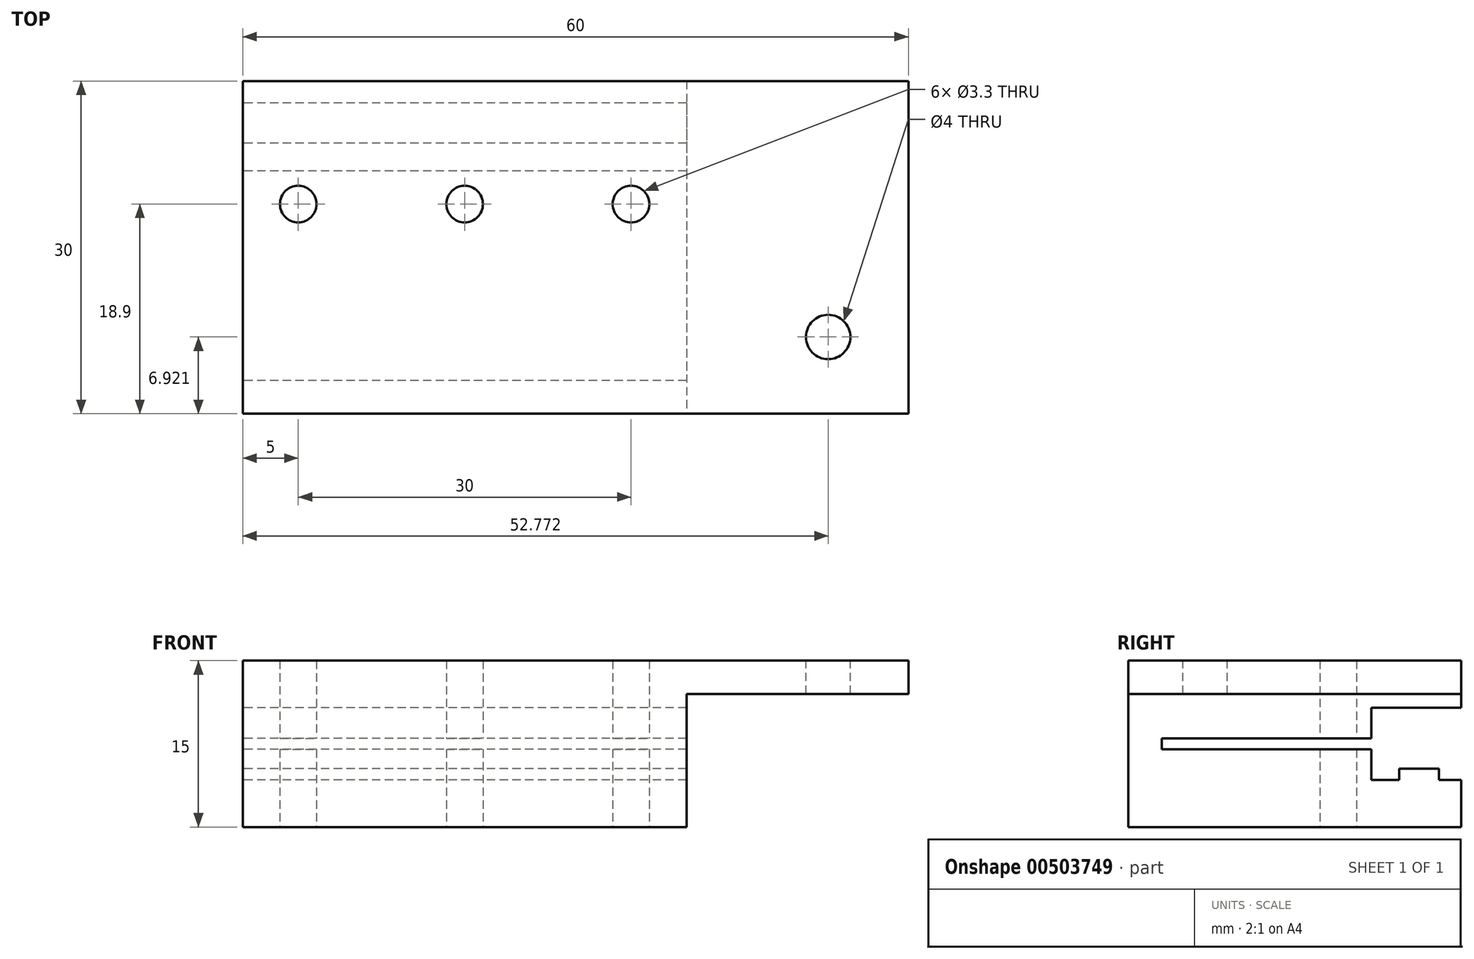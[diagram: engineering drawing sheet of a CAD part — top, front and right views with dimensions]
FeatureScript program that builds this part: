
annotation { "Feature Type Name" : "Feature", "Feature Type Description" : "" }
export const myFeature = defineFeature(function(context is Context, id is Id, definition is map)
    precondition{}
    {
        {
            var Q0;
            Q0=qCreatedBy(makeId("Front.planeOp"),FACE);
            var sketch = newSketch(context, id + "F0", { "sketchPlane" : qUnion([Q0])});
            skLineSegment(sketch, "E0.bottom", {"start": v(30, 7.5) * mm, "end": v(-30, 7.5) * mm});
            skLineSegment(sketch, "E0.top", {"start": v(30, -7.5) * mm, "end": v(-30, -7.5) * mm});
            skLineSegment(sketch, "E0.left", {"start": v(30, 7.5) * mm, "end": v(30, -7.5) * mm});
            skLineSegment(sketch, "E0.right", {"start": v(-30, 7.5) * mm, "end": v(-30, -7.5) * mm});
            skPoint(sketch, "E0.middle", {"position": v(0, 0) * mm});
            skSolve(sketch);
        }
        {
            var Q0;
            Q0 = qSketchRegion(id + "F0", true);
            extrude(context, id + "F1", {"entities" : qUnion([Q0]), "depth" : 30 * mm});
        }
        {
            var Q0;
            Q0=makeQuery(id+"F1.opExtrude","SWEPT_FACE",FACE,{"disambiguationData":[OSD([sQuery(id+"F0.wireOp",EDGE,"E0.right")])]});
            var sketch = newSketch(context, id + "F2", { "sketchPlane" : qUnion([Q0])});
            skLineSegment(sketch, "E1.bottom", {"start": v(0, 3.25) * mm, "end": v(8.1, 3.25) * mm});
            skLineSegment(sketch, "E1.top", {"start": v(0, -3.25) * mm, "end": v(2, -3.25) * mm});
            skLineSegment(sketch, "E1.left", {"start": v(0, 3.25) * mm, "end": v(0, -3.25) * mm});
            skLineSegment(sketch, "E1.right", {"start": v(8.1, 3.25) * mm, "end": v(8.1, 0.5) * mm});
            skLineSegment(sketch, "E2.bottom", {"start": v(8.1, 0.5) * mm, "end": v(27, 0.5) * mm});
            skLineSegment(sketch, "E2.top", {"start": v(8.1, -0.5) * mm, "end": v(27, -0.5) * mm});
            skLineSegment(sketch, "E2.right", {"start": v(27, 0.5) * mm, "end": v(27, -0.5) * mm});
            skLineSegment(sketch, "E3.trimOffspring", {"start": v(8.1, -0.5) * mm, "end": v(8.1, -3.25) * mm});
            skLineSegment(sketch, "E4.top", {"start": v(2, -2.25) * mm, "end": v(5.6, -2.25) * mm});
            skLineSegment(sketch, "E4.left", {"start": v(2, -3.25) * mm, "end": v(2, -2.25) * mm});
            skLineSegment(sketch, "E4.right", {"start": v(5.6, -3.25) * mm, "end": v(5.6, -2.25) * mm});
            skLineSegment(sketch, "E5.trimOffspring", {"start": v(5.6, -3.25) * mm, "end": v(8.1, -3.25) * mm});
            skSolve(sketch);
        }
        {
            var Q0;
            Q0 = qSketchRegion(id + "F2", true);
            extrude(context, id + "F3", {"entities" : qUnion([Q0]), "operationType" : NewBodyOperationType.REMOVE, "endBound" : BoundingType.THROUGH_ALL, "oppositeDirection" : true, "depth" : 25 * mm});
        }
        {
            var Q0;
            Q0=makeQuery(id+"F1.opExtrude","CAP_FACE",FACE,{"disambiguationData":[OSD([sQuery(id+"F0.wireOp",EDGE,"E0.bottom"),sQuery(id+"F0.wireOp",EDGE,"E0.top"),sQuery(id+"F0.wireOp",EDGE,"E0.left"),sQuery(id+"F0.wireOp",EDGE,"E0.right")])],"isStart":false});
            var sketch = newSketch(context, id + "F4", { "sketchPlane" : qUnion([Q0])});
            skLineSegment(sketch, "E6.bottom", {"start": v(30, -7.5) * mm, "end": v(10, -7.5) * mm});
            skLineSegment(sketch, "E6.top", {"start": v(30, 4.5) * mm, "end": v(10, 4.5) * mm});
            skLineSegment(sketch, "E6.left", {"start": v(30, -7.5) * mm, "end": v(30, 4.5) * mm});
            skLineSegment(sketch, "E6.right", {"start": v(10, -7.5) * mm, "end": v(10, 4.5) * mm});
            skSolve(sketch);
        }
        {
            var Q0;
            Q0 = qSketchRegion(id + "F4", true);
            extrude(context, id + "F5", {"entities" : qUnion([Q0]), "operationType" : NewBodyOperationType.REMOVE, "endBound" : BoundingType.THROUGH_ALL, "oppositeDirection" : true, "depth" : 25 * mm});
        }
        {
            var Q0;
            Q0=makeQuery(id+"F1.opExtrude","SWEPT_FACE",FACE,{"disambiguationData":[OSD([sQuery(id+"F0.wireOp",EDGE,"E0.top")])]});
            var sketch = newSketch(context, id + "F6", { "sketchPlane" : qUnion([Q0])});
            skCircle(sketch, "E7", {"center": v(5, 11.1) * mm, "radius": 1.65 * mm});
            skCircle(sketch, "E8", {"center": v(-25, 11.1) * mm, "radius": 1.65 * mm});
            skCircle(sketch, "E9", {"center": v(-10, 11.1) * mm, "radius": 1.65 * mm});
            skSolve(sketch);
        }
        {
            var Q0;
            Q0 = qSketchRegion(id + "F6", true);
            extrude(context, id + "F7", {"entities" : qUnion([Q0]), "operationType" : NewBodyOperationType.REMOVE, "endBound" : BoundingType.THROUGH_ALL, "oppositeDirection" : true, "depth" : 40 * mm, "offsetDistance" : 25 * mm});
        }
        {
            var Q0;
            Q0=makeQuery(id+"F1.opExtrude","SWEPT_FACE",FACE,{"disambiguationData":[OSD([sQuery(id+"F0.wireOp",EDGE,"E0.bottom")])]});
            var sketch = newSketch(context, id + "F8", { "sketchPlane" : qUnion([Q0])});
            skCircle(sketch, "E10", {"center": v(22.77, -23.08) * mm, "radius": 2 * mm});
            skSolve(sketch);
        }
        {
            var Q0;
            Q0 = qSketchRegion(id + "F8", true);
            extrude(context, id + "F9", {"entities" : qUnion([Q0]), "operationType" : NewBodyOperationType.REMOVE, "endBound" : BoundingType.THROUGH_ALL, "oppositeDirection" : true, "depth" : 25 * mm, "offsetDistance" : 25 * mm});
        }
    });
